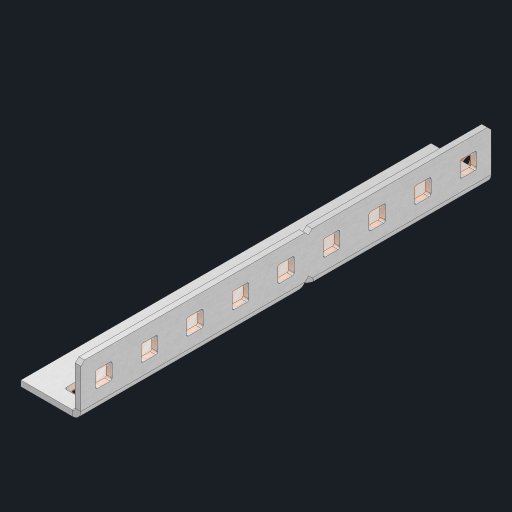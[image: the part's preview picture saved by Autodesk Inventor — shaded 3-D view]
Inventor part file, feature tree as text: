
AUTODESK INVENTOR PART (.ipt)
format: ipt  version: 2023 (Build 270158000, 158)  size: 559,616 bytes
history: native  units: in
note: dims shown in document units (in); Inventor stores cm internally (conversion verified against a paired STEP export)
features: other x23, extrude x17, sheet_metal_op x10, sketch x8, mirror x1, pattern_linear x1, chamfer x1
ambient origin geometry x8: Origin, YZ Plane, XZ Plane, XY Plane, X Axis, Y Axis, Z Axis, Center Point
bodies: Solid1 (feature_tree), Body (feature_tree)
feature tree (61):
  other  "Flange Pattern Plane"
  sheet_metal_op  "Flange Pattern"
  sheet_metal_op  "Body Pattern"
  other  "Arc Length"
  mirror  "Notch Mirror"
  pattern_linear  "Notch Pattern"  Spacing1=0.25in  [1 undecoded]
  chamfer  "End Chamfer"
  extrude  "Half Cut"  Depth=0.0625in
  sketch  "Sketch1"  dims[d0=1.5in]
  other  "Plate1"
  sketch  "Sketch2"  dims[d1=4.5in]
  other  "Plate2"
  sheet_metal_op  "Bend1"
  sheet_metal_op  "Corner1"
  sketch  "Sketch3"  dims[d2=0.0625in]
  other  "Flange Pattern Sketch"
  sketch  "Sketch7"  dims[d3=0.0625in]
  other  "Srf1"
  other  "Srf2"
  sketch  "Sketch8"  dims[d4=0.0312in]
  sketch  "Sketch9"  dims[d5=0.125in]
  other  "Srf91"
  sheet_metal_op  "Body Pattern Sketch"
  other  "Srf92"
  sketch  "Sketch13"  dims[d6=0.0625in]
  sketch  "Sketch14"  dims[d7=0.5in d8=90.0deg d9=0.0312in d10=0.25in d11=0.0625in d12=0.0625in d16=0.182in d17=0.02in d18=0.0625in d19=0.0in d20=0.25in d21=0.25in d46=0.172in d47=1.0in d48=0.0in d49=0.182in d50=0.02in d51=0.25in d52=0.25in d53=0.0625in d54=0.0in d55=0.172in d56=1.0in d57=0.0in d60=3.5433in d62=0.5in d63=0.3937in d65=0.5in d85=0.1473in d86=0.1782in d88=0.04in d89=0.0625in d90=0.0in d91=0.04in d92=0.0491in d95=2.5in d96=0.04in d97=0.25in d98=45.0deg d101=0.0in d102=2.497in d131=0.5in d132=3.5433in d134=0.5in d139=0.5in]
  other  "Srf856"
  other  "Srf1310"
  other  "Srf1311"
  other  "Srf1312"
  other  "Srf1376"
  other  "Srf1377"
  other  "Srf1728"
  other  "Srf1755"
  other  "Srf1878"
  other  "Srf1879"
  other  "Srf1880"
  other  "Srf1942"
  other  "Srf1943"
  other  "Srf1944"
  sheet_metal_op  "Flange Stamp"
  sheet_metal_op  "Flange Circle"
  sheet_metal_op  "Body Stamp"
  sheet_metal_op  "Body Circle"
  sheet_metal_op  "Notch"
  extrude  "ExtrusionSrf2"  Depth=0.0625in
  extrude  "ExtrusionSrf92"  Depth=0.5in
  extrude  "ExtrusionSrf856"  Depth=0.02in
  extrude  "ExtrusionSrf1310"  Depth=0.0625in
  extrude  "ExtrusionSrf1311"  TaperAngle=0.0deg  [1 undecoded]
  extrude  "ExtrusionSrf1312"  Depth=0.5in
  extrude  "ExtrusionSrf1376"  Depth=0.5in
  extrude  "ExtrusionSrf1377"  Depth=0.5in
  extrude  "ExtrusionSrf1728"  Depth=0.5in TaperAngle=0.0deg
  extrude  "ExtrusionSrf1755"  Depth=0.5in
  extrude  "ExtrusionSrf1878"  Depth=0.02in
  extrude  "ExtrusionSrf1879"  Depth=0.5in
  extrude  "ExtrusionSrf1880"  Depth=0.5in
  extrude  "ExtrusionSrf1942"  Depth=0.0625in
  extrude  "ExtrusionSrf1943"  TaperAngle=0.0deg  [1 undecoded]
  extrude  "ExtrusionSrf1944"  Depth=0.5in
note: 3 required parameter values undecoded (feature->parameter linkage not recoverable at this tier; creation-order binding heuristic only, values carry confidence <= 0.55)
